# Revit family: Digital_Media-Honeywell-VARIODYN_D1-583940(41)
name_source: partatom
category: Electrical Equipment
revit_build: Autodesk Revit 2017 (Build: 20160225_1515(x64)
units: mm (PartAtom-declared; Revit-internal decimal feet)

## family parameters
Cut with Voids When Loaded = No
Host = Face
OmniClass Number = 23.85.50.00
OmniClass Title = Communication Systems
Part Type = Equipment Switch
Room Calculation Point = No
Round Connector Dimension = Use Diameter
Shared = No

## types (2) — shared parameters
Air Humidity = 15 ... 90 %
Ambient Temperature = -5 °C ... 55 °C
Apparent Load = 0 VA
Default Elevation = 1219 mm
Depth = 345 mm  [stored 1.13189 ft]
Finish = Metal - Honeywell - Stainless Steel - Black
Frequency = 50 Hz
Height = 133 mm  [stored 0.436352 ft]
Load Sub-Classification = No
Manufacturer = Honeywell International
Manufacturer Fax Number = 02131/40615-606
Number of Poles = 1
Power Consumption = 50 / 80 W
Power Factor = 1
Product Documentation Link = https://www.esser-systems.com
Product Name = VARIODYN D1 Comprio
Product Page URL = https://www.esser-systems.com
Rated Load Current = 100 A
Rated Voltage = 24 V DC
Storage Temperature = -10 °C ... 60 °C
URL = www.esser-systems.com
Utility = No
Version = 2017 - v1.0a
Voltage = 24
Wattage = 50 W
Watts = 50 W
Width = 483 mm

## per-type parameters (varying)
| type | Constraints | Description | Model | Weight |
| D1 Comprio 4-8 - 583940 | 1 | VARIODYN D1 Comprio 4-8 (Stand alone without Ethernet) | 583940 | 5.70 kgf |
| D1 Comprio 4-24 - 583941 | 2 | VARIODYN D1 Comprio 4-24 (Stand alone without Ethernet) | 583941 | 6.80 kgf |

note: [stored X ft] marks values corroborated as IEEE doubles in the binary element streams (Revit-internal decimal feet)

## geometry (parser evidence)
native form markers: Sweep x4
no freeform markers — native parametric forms only
